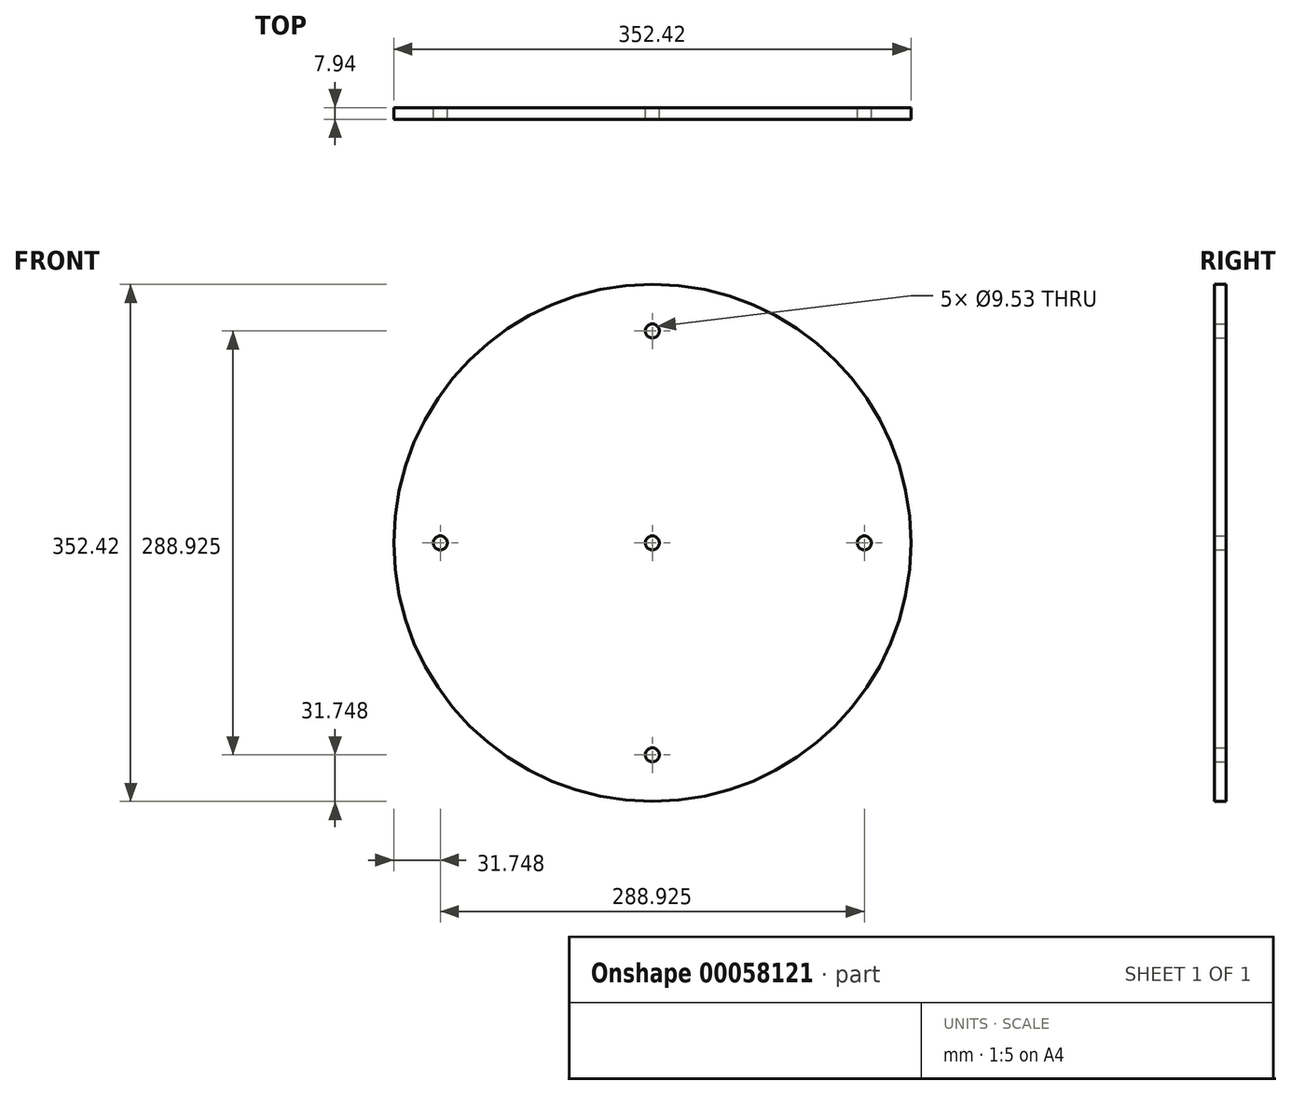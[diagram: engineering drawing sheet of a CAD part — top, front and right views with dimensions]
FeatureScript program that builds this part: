
annotation { "Feature Type Name" : "Feature", "Feature Type Description" : "" }
export const myFeature = defineFeature(function(context is Context, id is Id, definition is map)
    precondition{}
    {
        {
            var Q0;
            Q0=qCreatedBy(makeId("Front.planeOp"),FACE);
            var sketch = newSketch(context, id + "F0", { "sketchPlane" : qUnion([Q0])});
            skCircle(sketch, "E0", {"center": v(0, 0) * mm, "radius": 4.76 * mm});
            skCircle(sketch, "E1", {"center": v(0, 0) * mm, "radius": 176.21 * mm});
            skCircle(sketch, "E2", {"center": v(0, 144.46) * mm, "radius": 4.76 * mm});
            skCircle(sketch, "E3.1.0", {"center": v(-144.46, 0) * mm, "radius": 4.76 * mm});
            skCircle(sketch, "E3.2.0", {"center": v(0, -144.46) * mm, "radius": 4.76 * mm});
            skCircle(sketch, "E3.3.0", {"center": v(144.46, 0) * mm, "radius": 4.76 * mm});
            skSolve(sketch);
        }
        {
            var Q0;
            Q0=makeQuery(id+"F0.imprint","IMPRINT",FACE,{"disambiguationData":[TD([[makeQuery(id+"F0.imprint","IMPRINT",EDGE,{"derivedFrom":sQuery(id+"F0.wireOp",EDGE,"E0")}),-1.0]])]});
            extrude(context, id + "F1", {"entities" : qUnion([Q0]), "depth" : 7.94 * mm});
        }
    });
